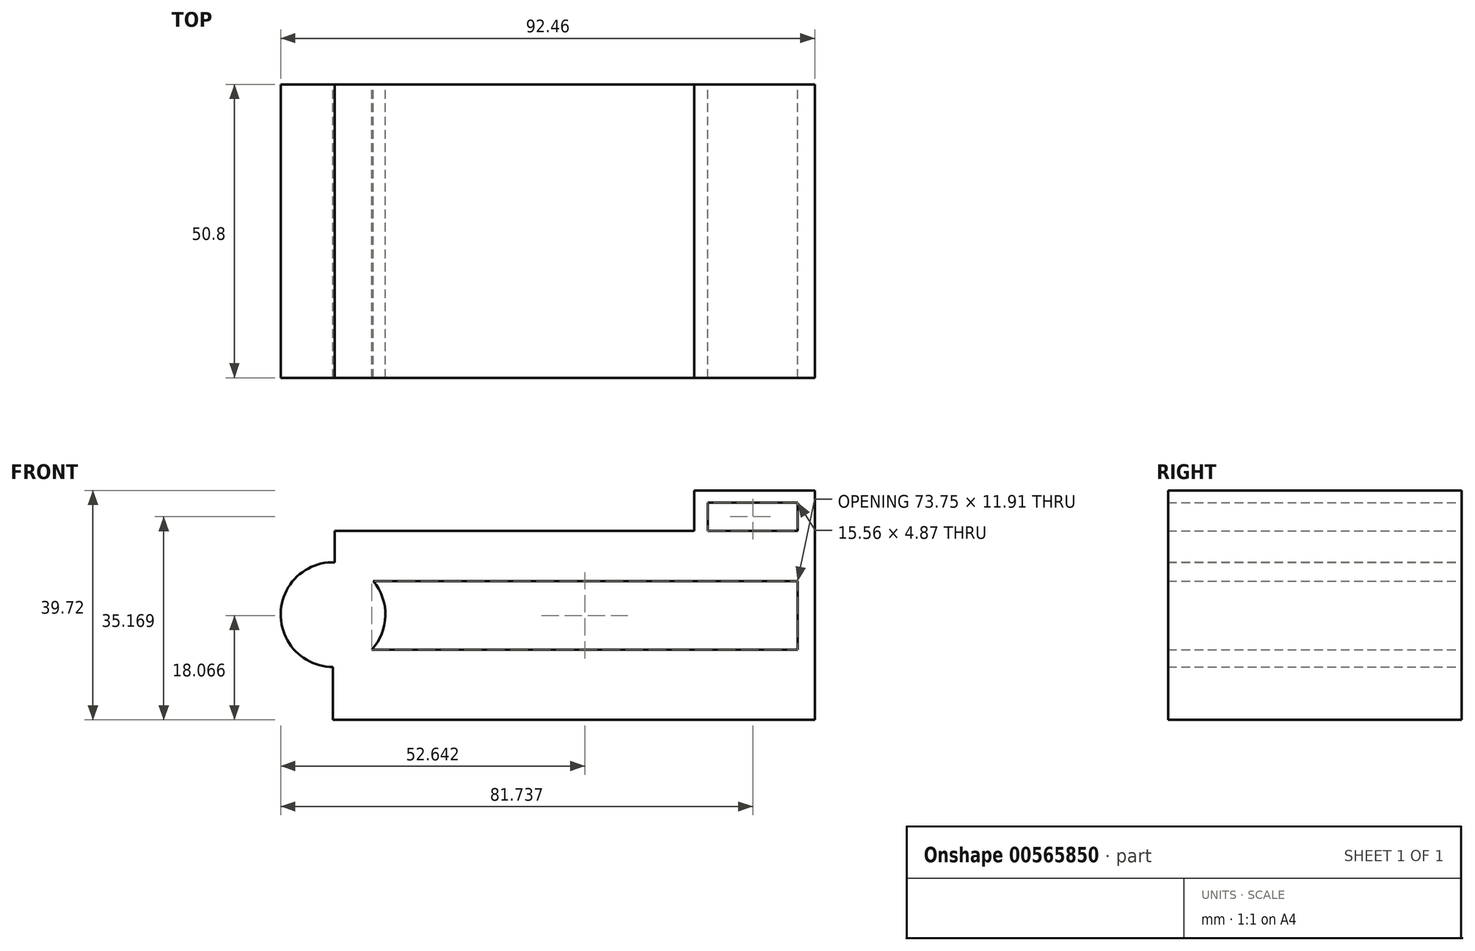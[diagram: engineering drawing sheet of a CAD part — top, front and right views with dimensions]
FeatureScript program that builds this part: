
annotation { "Feature Type Name" : "Feature", "Feature Type Description" : "" }
export const myFeature = defineFeature(function(context is Context, id is Id, definition is map)
    precondition{}
    {
        {
            var Q0;
            Q0=qCreatedBy(makeId("Front.planeOp"),FACE);
            var sketch = newSketch(context, id + "F0", { "sketchPlane" : qUnion([Q0])});
            skCircle(sketch, "E0", {"center": v(-47.75, 6.1) * mm, "radius": 9.07 * mm});
            skLineSegment(sketch, "E1.bottom", {"start": v(-47.44, 20.62) * mm, "end": v(32.7, 20.62) * mm});
            skLineSegment(sketch, "E1.top", {"start": v(-47.44, 11.91) * mm, "end": v(32.7, 11.91) * mm});
            skLineSegment(sketch, "E1.left", {"start": v(-47.44, 20.62) * mm, "end": v(-47.44, 11.91) * mm});
            skLineSegment(sketch, "E1.right", {"start": v(32.7, 20.62) * mm, "end": v(32.7, 11.91) * mm});
            skLineSegment(sketch, "E2.bottom", {"start": v(-47.75, 0) * mm, "end": v(32.7, 0) * mm});
            skLineSegment(sketch, "E2.top", {"start": v(-47.75, -12.1) * mm, "end": v(32.7, -12.1) * mm});
            skLineSegment(sketch, "E2.left", {"start": v(-47.75, 0) * mm, "end": v(-47.75, -12.1) * mm});
            skLineSegment(sketch, "E2.right", {"start": v(32.7, 0) * mm, "end": v(32.7, -12.1) * mm});
            skLineSegment(sketch, "E3.bottom", {"start": v(32.7, -12.1) * mm, "end": v(35.64, -12.1) * mm});
            skLineSegment(sketch, "E3.top", {"start": v(32.7, 25.5) * mm, "end": v(35.64, 25.5) * mm});
            skLineSegment(sketch, "E3.left", {"start": v(32.7, -12.1) * mm, "end": v(32.7, 25.5) * mm});
            skLineSegment(sketch, "E3.right", {"start": v(35.64, -12.1) * mm, "end": v(35.64, 25.5) * mm});
            skLineSegment(sketch, "E4.bottom", {"start": v(35.64, 25.5) * mm, "end": v(17.14, 25.5) * mm});
            skLineSegment(sketch, "E4.top", {"start": v(35.64, 27.61) * mm, "end": v(17.14, 27.61) * mm});
            skLineSegment(sketch, "E4.left", {"start": v(35.64, 25.5) * mm, "end": v(35.64, 27.61) * mm});
            skLineSegment(sketch, "E4.right", {"start": v(17.14, 25.5) * mm, "end": v(17.14, 27.61) * mm});
            skLineSegment(sketch, "E5.bottom", {"start": v(17.14, 27.61) * mm, "end": v(14.78, 27.61) * mm});
            skLineSegment(sketch, "E5.top", {"start": v(17.14, 20.62) * mm, "end": v(14.78, 20.62) * mm});
            skLineSegment(sketch, "E5.left", {"start": v(17.14, 27.61) * mm, "end": v(17.14, 20.62) * mm});
            skLineSegment(sketch, "E5.right", {"start": v(14.78, 27.61) * mm, "end": v(14.78, 20.62) * mm});
            skLineSegment(sketch, "E6.bottom", {"start": v(32.7, 20.62) * mm, "end": v(27.04, 20.62) * mm});
            skLineSegment(sketch, "E6.top", {"start": v(32.7, 20.62) * mm, "end": v(27.04, 20.62) * mm});
            skLineSegment(sketch, "E6.left", {"start": v(32.7, 20.62) * mm, "end": v(32.7, 20.62) * mm});
            skLineSegment(sketch, "E6.right", {"start": v(27.04, 20.62) * mm, "end": v(27.04, 20.62) * mm});
            skLineSegment(sketch, "E7.bottom", {"start": v(27.04, 20.62) * mm, "end": v(22.59, 20.62) * mm});
            skLineSegment(sketch, "E7.top", {"start": v(27.04, 25.5) * mm, "end": v(22.59, 25.5) * mm});
            skLineSegment(sketch, "E7.left", {"start": v(27.04, 20.62) * mm, "end": v(27.04, 25.5) * mm});
            skLineSegment(sketch, "E7.right", {"start": v(22.59, 20.62) * mm, "end": v(22.59, 25.5) * mm});
            skSolve(sketch);
        }
        {
            var Q0;
            Q0 = qSketchRegion(id + "F0", true);
            var Q1;
            Q1=makeQuery(id+"F0.imprint","IMPRINT",FACE,{"disambiguationData":[TD([[makeQuery(id+"F0.imprint","IMPRINT",EDGE,{"derivedFrom":sQuery(id+"F0.wireOp",EDGE,"E7.bottom")}),-1.0]])]});
            extrude(context, id + "F1", {"entities" : qUnion([Q0, Q1]), "endBound" : BoundingType.SYMMETRIC, "depth" : 50.8 * mm, "offsetDistance" : 25.4 * mm});
        }
    });
